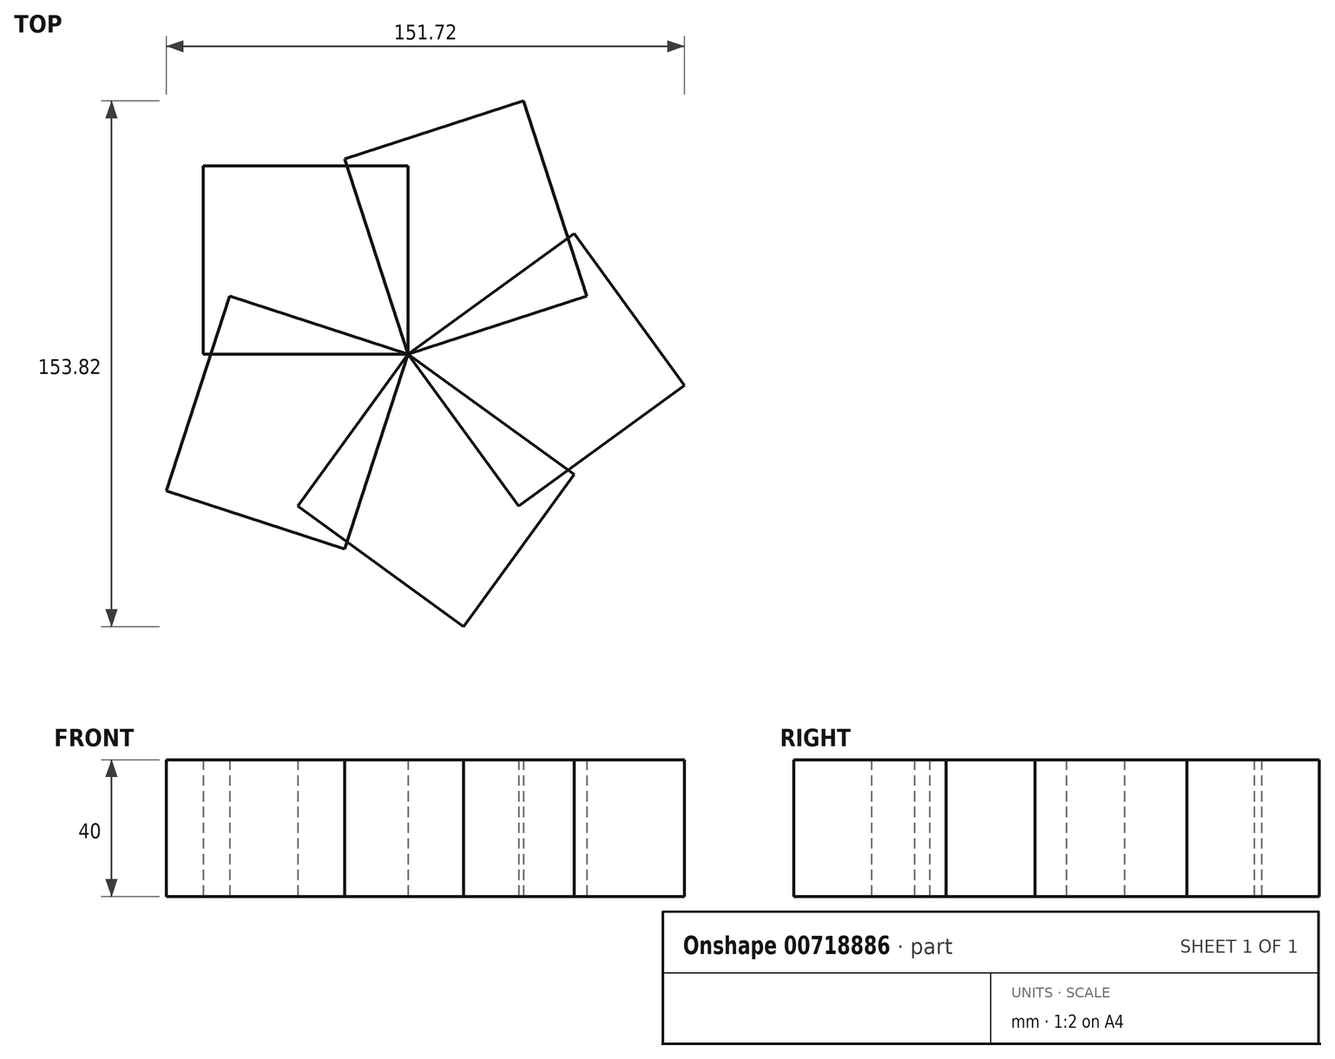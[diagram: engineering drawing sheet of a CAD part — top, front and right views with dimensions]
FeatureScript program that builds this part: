
annotation { "Feature Type Name" : "Feature", "Feature Type Description" : "" }
export const myFeature = defineFeature(function(context is Context, id is Id, definition is map)
    precondition{}
    {
        {
            var Q0;
            Q0=qCreatedBy(makeId("Top.planeOp"),FACE);
            var sketch = newSketch(context, id + "F0", { "sketchPlane" : qUnion([Q0])});
            skLineSegment(sketch, "E0.bottom", {"start": v(-60, 55) * mm, "end": v(0, 55) * mm});
            skLineSegment(sketch, "E0.top", {"start": v(-60, 0) * mm, "end": v(0, 0) * mm});
            skLineSegment(sketch, "E0.left", {"start": v(-60, 55) * mm, "end": v(-60, 0) * mm});
            skLineSegment(sketch, "E0.right", {"start": v(0, 55) * mm, "end": v(0, 0) * mm});
            skSolve(sketch);
        }
        {
            var Q0;
            Q0 = qSketchRegion(id + "F0", true);
            extrude(context, id + "F1", {"entities" : qUnion([Q0]), "depth" : 40 * mm, "offsetDistance" : 25 * mm});
        }
        {
            var Q0;
            Q0=makeQuery(id+"F1.opExtrude","SWEPT_BODY",BODY,{"disambiguationData":[OSD([sQuery(id+"F0.wireOp",EDGE,"E0.bottom"),sQuery(id+"F0.wireOp",EDGE,"E0.top"),sQuery(id+"F0.wireOp",EDGE,"E0.left"),sQuery(id+"F0.wireOp",EDGE,"E0.right")])]});
            var Q1;
            Q1=makeQuery(id+"F1.opExtrude","SWEPT_EDGE",EDGE,{"disambiguationData":[OSD([sQuery(id+"F0.wireOp",EDGE,"E0.top"),sQuery(id+"F0.wireOp",EDGE,"E0.right")])]});
            circularPattern(context, id + "F2", {"entities" : qUnion([Q0]), "axis" : qUnion([Q1]), "angle" : 360 * degree, "instanceCount" : 5, "equalSpace" : true});
        }
    });
